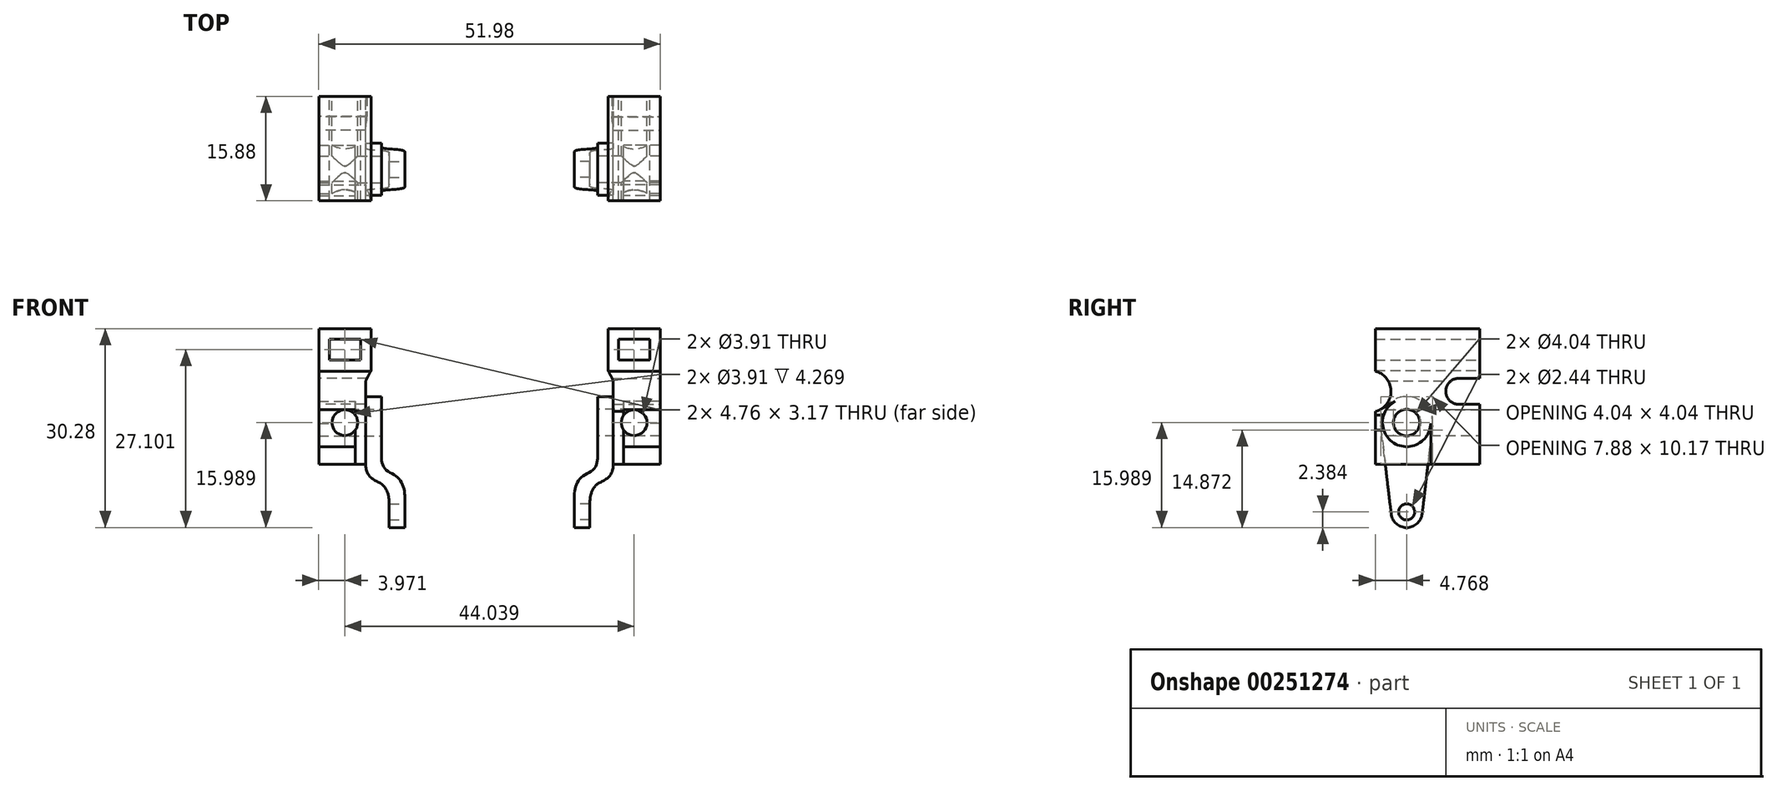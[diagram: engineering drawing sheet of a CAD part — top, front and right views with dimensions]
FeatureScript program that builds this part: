
annotation { "Feature Type Name" : "Feature", "Feature Type Description" : "" }
export const myFeature = defineFeature(function(context is Context, id is Id, definition is map)
    precondition{}
    {
        {
            var Q0;
            Q0=qCreatedBy(makeId("Front.planeOp"),FACE);
            var sketch = newSketch(context, id + "F0", { "sketchPlane" : qUnion([Q0])});
            skLineSegment(sketch, "E0", {"start": v(18.05, 32.8) * mm, "end": v(25.99, 32.8) * mm});
            skLineSegment(sketch, "E1", {"start": v(25.99, 32.8) * mm, "end": v(25.99, 23.28) * mm});
            skLineSegment(sketch, "E2", {"start": v(25.99, 23.28) * mm, "end": v(20.43, 23.28) * mm});
            skLineSegment(sketch, "E3", {"start": v(20.43, 23.28) * mm, "end": v(20.43, 12.17) * mm});
            skLineSegment(sketch, "E4", {"start": v(20.43, 12.17) * mm, "end": v(18.84, 12.17) * mm});
            skLineSegment(sketch, "E5", {"start": v(18.84, 12.17) * mm, "end": v(18.84, 24.87) * mm});
            skLineSegment(sketch, "E6", {"start": v(18.84, 24.87) * mm, "end": v(18.05, 26.46) * mm});
            skLineSegment(sketch, "E7", {"start": v(18.05, 32.8) * mm, "end": v(18.05, 26.46) * mm});
            skLineSegment(sketch, "E8.bottom", {"start": v(19.64, 31.22) * mm, "end": v(24.4, 31.22) * mm});
            skLineSegment(sketch, "E8.top", {"start": v(19.64, 28.04) * mm, "end": v(24.4, 28.04) * mm});
            skLineSegment(sketch, "E8.left", {"start": v(19.64, 31.22) * mm, "end": v(19.64, 28.04) * mm});
            skLineSegment(sketch, "E8.right", {"start": v(24.4, 31.22) * mm, "end": v(24.4, 28.04) * mm});
            skLineSegment(sketch, "E9", {"start": v(18.84, 23.28) * mm, "end": v(16.46, 23.28) * mm});
            skLineSegment(sketch, "E10", {"start": v(16.46, 23.28) * mm, "end": v(16.46, 6.73) * mm});
            skLineSegment(sketch, "E11", {"start": v(22.02, 32.8) * mm, "end": v(22.02, 5.2) * mm, "construction": true});
            skPoint(sketch, "E11.endSnap0", {"position": v(22.02, 28.04) * mm});
            skLineSegment(sketch, "E12", {"start": v(12.9, 12.67) * mm, "end": v(12.9, 2.53) * mm});
            skLineSegment(sketch, "E13", {"start": v(12.9, 2.53) * mm, "end": v(15.27, 2.53) * mm});
            skLineSegment(sketch, "E14", {"start": v(15.27, 2.53) * mm, "end": v(15.27, 9.81) * mm});
            skLineSegment(sketch, "E15", {"start": v(22.02, 5.2) * mm, "end": v(14.08, 5.2) * mm, "construction": true});
            skLineSegment(sketch, "E16", {"start": v(14.08, 5.2) * mm, "end": v(14.08, 20.14) * mm, "construction": true});
            skFitSpline(sketch, "E17", {"points": [v(15.27, 6.17) * mm, v(16.46, 9.18) * mm, v(18.84, 12.32) * mm], "startDerivative": vector(0, 8.88) * mm, "endDerivative": vector(0, 13.63) * mm});
            skFitSpline(sketch, "E18", {"points": [v(12.9, 7.06) * mm, v(14.37, 10.49) * mm, v(16.46, 13.4) * mm], "startDerivative": vector(0, 10.4) * mm, "endDerivative": vector(0, 13.7) * mm});
            skSolve(sketch);
        }
        {
            var Q0;
            Q0=qSketchRegion(id+"F0",true);
            extrude(context, id + "F1", {"entities" : qUnion([Q0]), "depth" : 15.88 * mm});
        }
        {
            var Q0;
            Q0=makeQuery(id+"F1.opExtrude","CAP_FACE",FACE,{"disambiguationData":[OSD([sQuery(id+"F0.wireOp",EDGE,"E0"),sQuery(id+"F0.wireOp",EDGE,"E1"),sQuery(id+"F0.wireOp",EDGE,"E2"),sQuery(id+"F0.wireOp",EDGE,"E3"),sQuery(id+"F0.wireOp",EDGE,"E4"),sQuery(id+"F0.wireOp",EDGE,"E5"),sQuery(id+"F0.wireOp",EDGE,"E6"),sQuery(id+"F0.wireOp",EDGE,"E7"),sQuery(id+"F0.wireOp",EDGE,"E8.bottom"),sQuery(id+"F0.wireOp",EDGE,"E8.top"),sQuery(id+"F0.wireOp",EDGE,"E8.left"),sQuery(id+"F0.wireOp",EDGE,"E8.right"),sQuery(id+"F0.wireOp",EDGE,"E9"),sQuery(id+"F0.wireOp",EDGE,"E10"),sQuery(id+"F0.wireOp",EDGE,"E12"),sQuery(id+"F0.wireOp",EDGE,"E13"),sQuery(id+"F0.wireOp",EDGE,"E14"),sQuery(id+"F0.wireOp",EDGE,"E17"),sQuery(id+"F0.wireOp",EDGE,"E18")])],"isStart":true});
            var sketch = newSketch(context, id + "F2", { "sketchPlane" : qUnion([Q0])});
            skLineSegment(sketch, "E19", {"start": v(-18.84, 23.28) * mm, "end": v(-18.84, 12.32) * mm});
            skSolve(sketch);
        }
        {
            var Q0;
            Q0=qSketchRegion(id+"F2",true);
            var Q1;
            Q1=makeQuery(id+"F2.imprint","IMPRINT",FACE,{"disambiguationData":[TD([[makeQuery(id+"F2.imprint","IMPRINT",EDGE,{"derivedFrom":sQuery(id+"F2.wireOp",EDGE,"E19")}),1.0]])]});
            extrude(context, id + "F3", {"entities" : qUnion([Q0, Q1]), "operationType" : NewBodyOperationType.REMOVE, "oppositeDirection" : true, "depth" : 6.35 * mm});
        }
        {
            var Q0;
            Q0=makeQuery(id+"F1.opExtrude","SWEPT_FACE",FACE,{"disambiguationData":[OSD([sQuery(id+"F0.wireOp",EDGE,"E10")])]});
            var sketch = newSketch(context, id + "F4", { "sketchPlane" : qUnion([Q0])});
            skCircle(sketch, "E20", {"center": v(11.11, 18.52) * mm, "radius": 2.02 * mm});
            skSolve(sketch);
        }
        {
            var Q0;
            Q0=qSketchRegion(id+"F4",true);
            extrude(context, id + "F5", {"entities" : qUnion([Q0]), "operationType" : NewBodyOperationType.REMOVE, "oppositeDirection" : true, "depth" : 6.35 * mm});
        }
        {
            var Q0;
            Q0=makeQuery(id+"F1.opExtrude","SWEPT_FACE",FACE,{"disambiguationData":[OSD([sQuery(id+"F0.wireOp",EDGE,"E12")])]});
            var sketch = newSketch(context, id + "F6", { "sketchPlane" : qUnion([Q0])});
            skCircle(sketch, "E21", {"center": v(11.11, 4.91) * mm, "radius": 1.22 * mm});
            skSolve(sketch);
        }
        {
            var Q0;
            Q0=qSketchRegion(id+"F6",true);
            extrude(context, id + "F7", {"entities" : qUnion([Q0]), "operationType" : NewBodyOperationType.REMOVE, "oppositeDirection" : true, "depth" : 3.17 * mm});
        }
        {
            var Q0;
            Q0=makeQuery(id+"F1.opExtrude","SWEPT_FACE",FACE,{"disambiguationData":[OSD([sQuery(id+"F0.wireOp",EDGE,"E12")])]});
            var sketch = newSketch(context, id + "F8", { "sketchPlane" : qUnion([Q0])});
            skCircle(sketch, "E22", {"center": v(11.11, 4.91) * mm, "radius": 2.38 * mm});
            skCircle(sketch, "E23", {"center": v(11.11, 18.52) * mm, "radius": 3.97 * mm});
            skLineSegment(sketch, "E24", {"start": v(7.17, 18.06) * mm, "end": v(8.75, 4.64) * mm});
            skLineSegment(sketch, "E25", {"start": v(15.05, 18.06) * mm, "end": v(13.48, 4.64) * mm});
            skLineSegment(sketch, "E26.bottom", {"start": v(5.27, 1.8) * mm, "end": v(17.26, 1.8) * mm});
            skLineSegment(sketch, "E26.top", {"start": v(5.27, 24.07) * mm, "end": v(17.26, 24.07) * mm});
            skLineSegment(sketch, "E26.left", {"start": v(5.27, 1.8) * mm, "end": v(5.27, 24.07) * mm});
            skLineSegment(sketch, "E26.right", {"start": v(17.26, 1.8) * mm, "end": v(17.26, 24.07) * mm});
            skSolve(sketch);
        }
        {
            var Q0;
            Q0=qSketchRegion(id+"F8",true);
            extrude(context, id + "F9", {"entities" : qUnion([Q0]), "operationType" : NewBodyOperationType.REMOVE, "oppositeDirection" : true, "depth" : 5.95 * mm});
        }
        {
            var Q0;
            {var subQ0=sQuery(id+"F0.wireOp",EDGE,"E5");Q0=makeQuery(id+"F9.boolean.opBoolean","MERGE",FACE,{"derivedFrom":[makeQuery(id+"F3.boolean.opBoolean","MERGE",FACE,{"derivedFrom":[makeQuery(id+"F1.opExtrude","SWEPT_FACE",FACE,{"disambiguationData":[OSD([subQ0]),TDD([makeQuery(id+"F0.imprint","IMPRINT",EDGE,{"disambiguationData":[TD([[makeQuery(id+"F0.imprint","INTERSECT",VERTEX,{"derivedFrom":[sQuery(id+"F0.wireOp",EDGE,"E4"),subQ0]}),-1.0]])],"derivedFrom":subQ0})])]}),makeQuery(id+"F1.opExtrude","SWEPT_FACE",FACE,{"disambiguationData":[OSD([subQ0]),TDD([makeQuery(id+"F0.imprint","IMPRINT",EDGE,{"disambiguationData":[TD([[makeQuery(id+"F0.imprint","INTERSECT",VERTEX,{"derivedFrom":[subQ0,sQuery(id+"F0.wireOp",EDGE,"E6")]}),1.0]])],"derivedFrom":subQ0})])]}),makeQuery(id+"F3.opExtrude","SWEPT_FACE",FACE,{"disambiguationData":[OSD([sQuery(id+"F2.wireOp",EDGE,"E19")])]})]}),makeQuery(id+"F9.opExtrude","CAP_FACE",FACE,{"disambiguationData":[OSD([sQuery(id+"F8.wireOp",EDGE,"E22"),sQuery(id+"F8.wireOp",EDGE,"E23"),sQuery(id+"F8.wireOp",EDGE,"E24"),sQuery(id+"F8.wireOp",EDGE,"E25"),sQuery(id+"F8.wireOp",EDGE,"E26.bottom"),sQuery(id+"F8.wireOp",EDGE,"E26.top"),sQuery(id+"F8.wireOp",EDGE,"E26.left"),sQuery(id+"F8.wireOp",EDGE,"E26.right")])],"isStart":false})]});}
            var sketch = newSketch(context, id + "F10", { "sketchPlane" : qUnion([Q0])});
            skCircle(sketch, "E27", {"center": v(3.18, 23.28) * mm, "radius": 1.98 * mm});
            skLineSegment(sketch, "E28", {"start": v(3.08, 25.26) * mm, "end": v(0, 25.26) * mm});
            skLineSegment(sketch, "E29", {"start": v(3.12, 21.3) * mm, "end": v(0, 21.3) * mm});
            skLineSegment(sketch, "E30", {"start": v(0, 25.26) * mm, "end": v(0, 21.3) * mm});
            skSolve(sketch);
        }
        {
            var Q0;
            Q0=qSketchRegion(id+"F10",true);
            extrude(context, id + "F11", {"entities" : qUnion([Q0]), "operationType" : NewBodyOperationType.REMOVE, "depth" : 25.4 * mm, "symmetric" : true});
        }
        {
            var Q0;
            Q0=makeQuery(id+"F1.opExtrude","SWEPT_FACE",FACE,{"disambiguationData":[OSD([sQuery(id+"F0.wireOp",EDGE,"E7")])]});
            var sketch = newSketch(context, id + "F12", { "sketchPlane" : qUnion([Q0])});
            skCircle(sketch, "E31", {"center": v(16.67, 23.28) * mm, "radius": 3.18 * mm});
            skSolve(sketch);
        }
        {
            var Q0;
            Q0=qSketchRegion(id+"F12",true);
            extrude(context, id + "F13", {"entities" : qUnion([Q0]), "operationType" : NewBodyOperationType.REMOVE, "oppositeDirection" : true, "depth" : 25.4 * mm});
        }
        {
            var Q0;
            Q0=qCreatedBy(makeId("Right.planeOp"),FACE);
            var sketch = newSketch(context, id + "F14", { "sketchPlane" : qUnion([Q0])});
            skLineSegment(sketch, "E32.bottom", {"start": v(-29.03, 45.11) * mm, "end": v(-6.29, 45.11) * mm});
            skLineSegment(sketch, "E32.top", {"start": v(-29.03, 24.7) * mm, "end": v(-6.29, 24.7) * mm});
            skLineSegment(sketch, "E32.left", {"start": v(-29.03, 45.11) * mm, "end": v(-29.03, 24.7) * mm});
            skLineSegment(sketch, "E32.right", {"start": v(-6.29, 45.11) * mm, "end": v(-6.29, 24.7) * mm});
            skSolve(sketch);
        }
        {
            var Q0;
            Q0=makeQuery(id+"F1.opExtrude","SWEPT_FACE",FACE,{"disambiguationData":[OSD([sQuery(id+"F0.wireOp",EDGE,"E3")])]});
            var sketch = newSketch(context, id + "F15", { "sketchPlane" : qUnion([Q0])});
            skCircle(sketch, "E33", {"center": v(-11.11, 18.52) * mm, "radius": 3.67 * mm});
            skLineSegment(sketch, "E34", {"start": v(-15.15, 20.5) * mm, "end": v(-12.87, 21.74) * mm});
            skLineSegment(sketch, "E35", {"start": v(-7.45, 18.66) * mm, "end": v(-7.45, 12.17) * mm});
            skSolve(sketch);
        }
        {
            var Q0;
            {var subQ0=sQuery(id+"F15.wireOp",EDGE,"E35");var subQ1=sQuery(id+"F15.wireOp",EDGE,"E33");var subQ2=makeQuery(id+"F15.imprint","INTERSECT",VERTEX,{"disambiguationData":[OD(0.0)],"derivedFrom":[subQ1,subQ0]});Q0=makeQuery(id+"F15.imprint","IMPRINT",FACE,{"disambiguationData":[TD([[makeQuery(id+"F15.imprint","IMPRINT",EDGE,{"disambiguationData":[TD([[subQ2,1.0]])],"derivedFrom":subQ1}),1.0]])]});}
            var Q1;
            {var subQ6=sQuery(id+"F15.wireOp",EDGE,"E34");Q1=makeQuery(id+"F15.imprint","IMPRINT",FACE,{"disambiguationData":[TD([[makeQuery(id+"F15.imprint","IMPRINT",EDGE,{"derivedFrom":subQ6}),1.0]])]});}
            extrude(context, id + "F16", {"entities" : qUnion([Q0, Q1]), "operationType" : NewBodyOperationType.ADD, "depth" : 5.56 * mm});
        }
        {
            var Q0;
            {var subQ0=sQuery(id+"F0.wireOp",EDGE,"E3");var subQ1=sQuery(id+"F0.wireOp",EDGE,"E6");var subQ2=sQuery(id+"F0.wireOp",EDGE,"E5");var subQ3=sQuery(id+"F0.wireOp",EDGE,"E9");var subQ4=sQuery(id+"F0.wireOp",EDGE,"E4");var subQ5=sQuery(id+"F0.wireOp",EDGE,"E17");Q0=makeQuery(id+"F16.boolean.opBoolean","MERGE",FACE,{"derivedFrom":[makeQuery(id+"F11.boolean.opBoolean","SPLIT",FACE,{"disambiguationData":[TD([makeQuery(id+"F1.opExtrude","SWEPT_FACE",FACE,{"disambiguationData":[OSD([subQ0])]})])],"derivedFrom":makeQuery(id+"F1.opExtrude","CAP_FACE",FACE,{"disambiguationData":[OSD([sQuery(id+"F0.wireOp",EDGE,"E0"),sQuery(id+"F0.wireOp",EDGE,"E1"),sQuery(id+"F0.wireOp",EDGE,"E2"),subQ0,subQ4,subQ2,subQ1,sQuery(id+"F0.wireOp",EDGE,"E7"),sQuery(id+"F0.wireOp",EDGE,"E8.bottom"),sQuery(id+"F0.wireOp",EDGE,"E8.top"),sQuery(id+"F0.wireOp",EDGE,"E8.left"),sQuery(id+"F0.wireOp",EDGE,"E8.right"),subQ3,sQuery(id+"F0.wireOp",EDGE,"E10"),sQuery(id+"F0.wireOp",EDGE,"E12"),sQuery(id+"F0.wireOp",EDGE,"E13"),sQuery(id+"F0.wireOp",EDGE,"E14"),subQ5,sQuery(id+"F0.wireOp",EDGE,"E18")])],"isStart":true})}),makeQuery(id+"F16.opExtrude","SWEPT_FACE",FACE,{"disambiguationData":[OSD([subQ0])]})]});}
            var sketch = newSketch(context, id + "F17", { "sketchPlane" : qUnion([Q0])});
            skCircle(sketch, "E36", {"center": v(-22.02, 18.52) * mm, "radius": 1.96 * mm});
            skSolve(sketch);
        }
        {
            var Q0;
            Q0 = qSketchRegion(id + "F17", true);
            extrude(context, id + "F18", {"entities" : qUnion([Q0]), "operationType" : NewBodyOperationType.REMOVE, "oppositeDirection" : true, "depth" : 25.4 * mm});
        }
        {
            var Q0;
            Q0=makeQuery(id+"F1.opExtrude","SWEPT_BODY",BODY,{"disambiguationData":[OSD([sQuery(id+"F0.wireOp",EDGE,"E0"),sQuery(id+"F0.wireOp",EDGE,"E1"),sQuery(id+"F0.wireOp",EDGE,"E2"),sQuery(id+"F0.wireOp",EDGE,"E3"),sQuery(id+"F0.wireOp",EDGE,"E4"),sQuery(id+"F0.wireOp",EDGE,"E5"),sQuery(id+"F0.wireOp",EDGE,"E6"),sQuery(id+"F0.wireOp",EDGE,"E7"),sQuery(id+"F0.wireOp",EDGE,"E8.bottom"),sQuery(id+"F0.wireOp",EDGE,"E8.top"),sQuery(id+"F0.wireOp",EDGE,"E8.left"),sQuery(id+"F0.wireOp",EDGE,"E8.right"),sQuery(id+"F0.wireOp",EDGE,"E9"),sQuery(id+"F0.wireOp",EDGE,"E10"),sQuery(id+"F0.wireOp",EDGE,"E12"),sQuery(id+"F0.wireOp",EDGE,"E13"),sQuery(id+"F0.wireOp",EDGE,"E14"),sQuery(id+"F0.wireOp",EDGE,"E17"),sQuery(id+"F0.wireOp",EDGE,"E18")])]});
            var Q1;
            Q1=makeQuery(id+"F14.imprint","IMPRINT",FACE,{"disambiguationData":[TD([[makeQuery(id+"F14.imprint","IMPRINT",EDGE,{"derivedFrom":sQuery(id+"F14.wireOp",EDGE,"E32.bottom")}),-1.0]])]});
            mirror(context, id + "F19", {"entities" : qUnion([Q0]), "mirrorPlane" : qUnion([Q1])});
        }
    });
